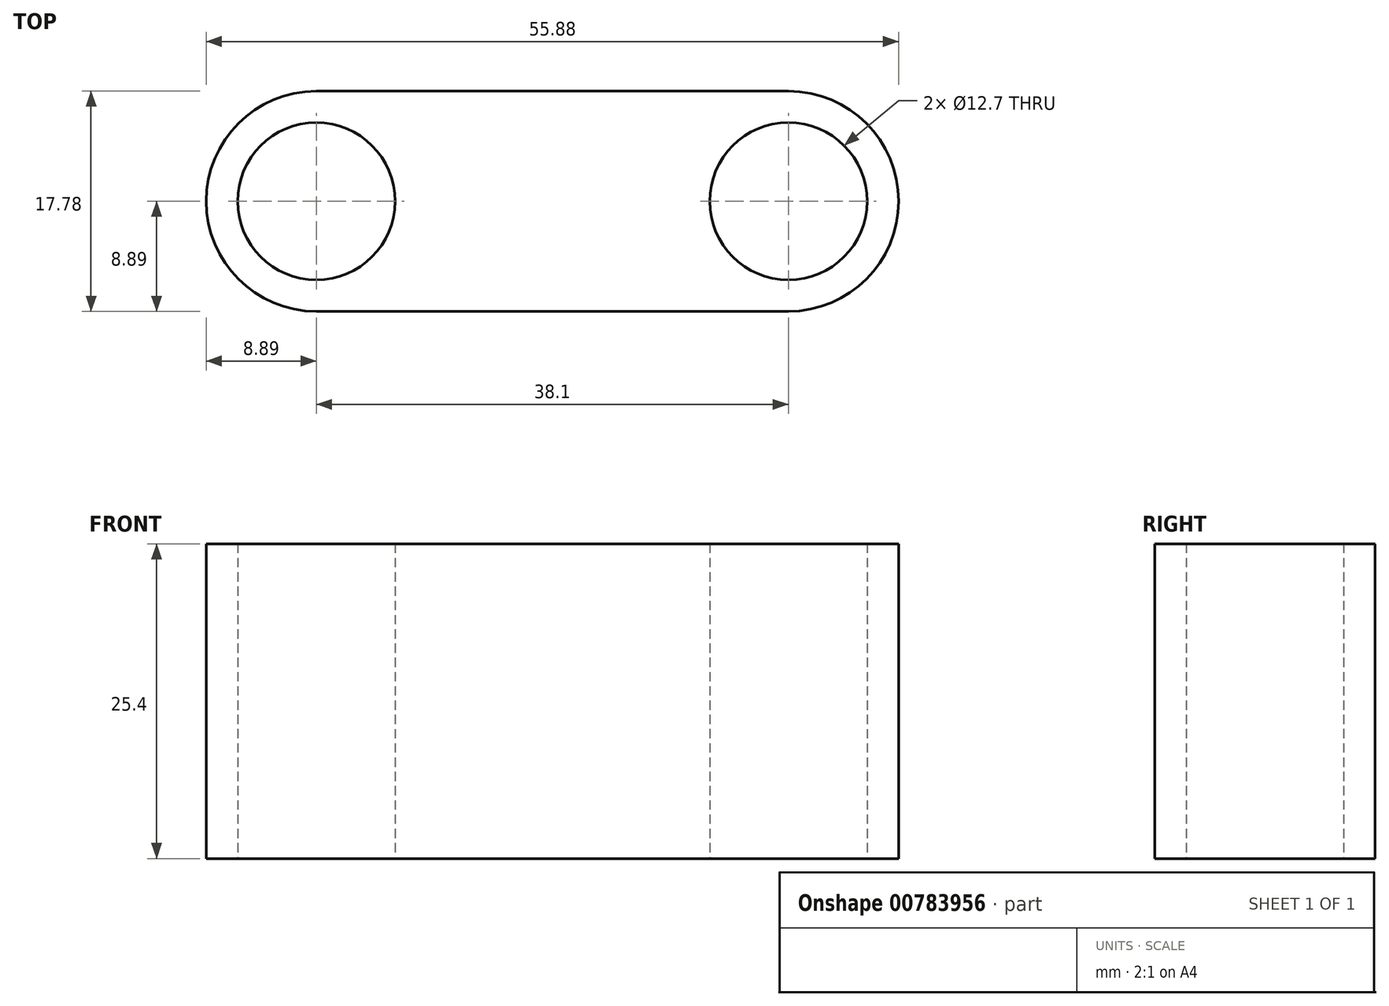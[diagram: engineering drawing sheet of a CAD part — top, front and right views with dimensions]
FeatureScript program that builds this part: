
annotation { "Feature Type Name" : "Feature", "Feature Type Description" : "" }
export const myFeature = defineFeature(function(context is Context, id is Id, definition is map)
    precondition{}
    {
        {
            var Q0;
            Q0=qCreatedBy(makeId("Top.planeOp"),FACE);
            var sketch = newSketch(context, id + "F0", { "sketchPlane" : qUnion([Q0])});
            skCircle(sketch, "E0", {"center": v(0, 0) * mm, "radius": 6.35 * mm});
            skCircle(sketch, "E1", {"center": v(38.1, 0) * mm, "radius": 6.35 * mm});
            skCircle(sketch, "E2", {"center": v(0, 0) * mm, "radius": 8.9 * mm});
            skCircle(sketch, "E3", {"center": v(38.1, 0) * mm, "radius": 8.9 * mm});
            skLineSegment(sketch, "E4", {"start": v(0, 8.9) * mm, "end": v(38.1, 8.89) * mm});
            skLineSegment(sketch, "E5", {"start": v(0, -8.9) * mm, "end": v(38.1, -8.89) * mm});
            skSolve(sketch);
        }
        {
            var Q0;
            Q0 = qSketchRegion(id + "F0", true);
            extrude(context, id + "F1", {"entities" : qUnion([Q0]), "depth" : 25.4 * mm, "offsetDistance" : 25.4 * mm});
        }
    });
